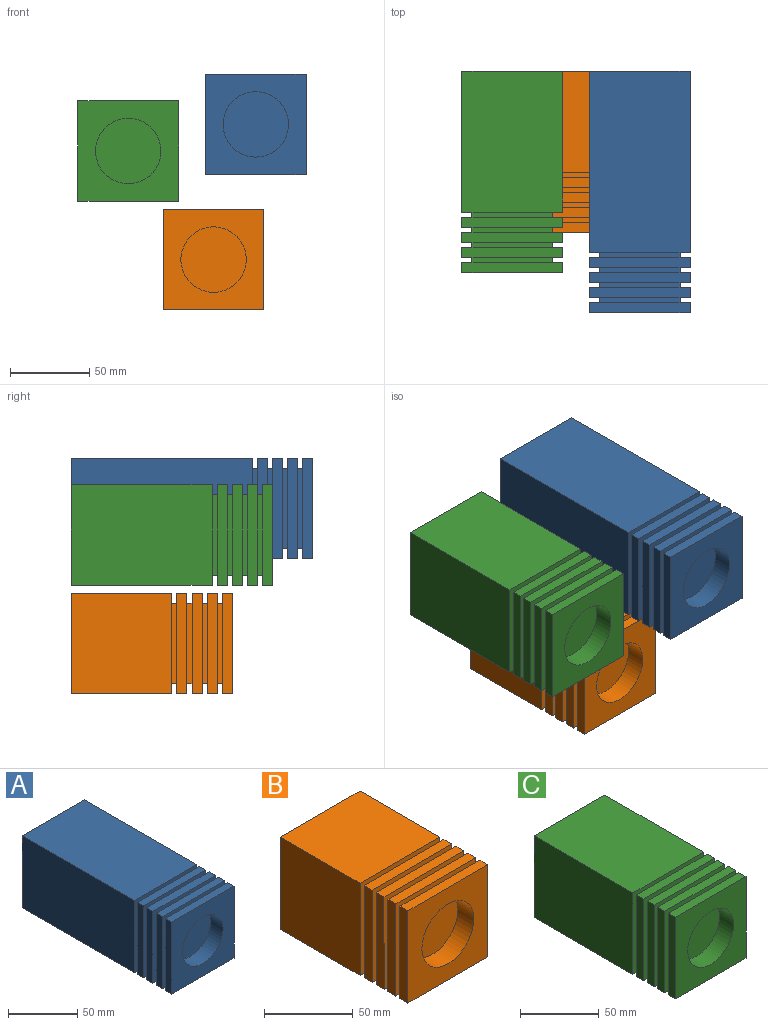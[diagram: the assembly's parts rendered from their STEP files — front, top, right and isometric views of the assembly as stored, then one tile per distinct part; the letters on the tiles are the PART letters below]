
ASSEMBLY  parts=3 mates=2
PART A: 48 faces, bbox 63.5x152.4x63.5 mm
  f0: plane 114.3x63.5mm, normal (1,0,0), area 7258.1mm2, adj f1,f2,f8,f41
  f1: plane 114.3x63.5mm, normal (0,0,-1), area 7258.1mm2, adj f0,f3,f8,f41
  f2: plane 114.3x63.5mm, normal (0,0,1), area 7258.1mm2, adj f0,f3,f8,f41
  f3: plane 114.3x63.5mm, normal (-1,0,0), area 7258.1mm2, adj f1,f2,f8,f41
  f4: plane 50.8x3.18mm, normal (0,0,1), area 161.3mm2, adj f5,f6,f7,f8
  f5: plane 50.8x3.18mm, normal (-1,0,0), area 161.3mm2, adj f4,f7,f8,f9
  f6: plane 50.8x3.18mm, normal (1,0,0), area 161.3mm2, adj f4,f7,f8,f9
  f7: plane 63.5x63.5mm, normal (0,1,0), area 1451.6mm2, adj f4,f5,f6,f9,f10,f11,f12,f13
  f8: plane 63.5x63.5mm, normal (0,-1,0), area 1451.6mm2, adj f0,f1,f2,f3,f4,f5,f6,f9
  f9: plane 50.8x3.18mm, normal (0,0,-1), area 161.3mm2, adj f5,f6,f7,f8
  f10: plane 63.5x6.35mm, normal (1,0,0), area 403.2mm2, adj f7,f11,f12,f18
  f11: plane 63.5x6.35mm, normal (0,0,-1), area 403.2mm2, adj f7,f10,f13,f18
  f12: plane 63.5x6.35mm, normal (0,0,1), area 403.2mm2, adj f7,f10,f13,f18
  f13: plane 63.5x6.35mm, normal (-1,0,0), area 403.2mm2, adj f7,f11,f12,f18
  f14: plane 50.8x3.18mm, normal (0,0,1), area 161.3mm2, adj f15,f16,f17,f18
  f15: plane 50.8x3.18mm, normal (-1,0,0), area 161.3mm2, adj f14,f17,f18,f19
  f16: plane 50.8x3.18mm, normal (1,0,0), area 161.3mm2, adj f14,f17,f18,f19
  f17: plane 63.5x63.5mm, normal (0,1,0), area 1451.6mm2, adj f14,f15,f16,f19,f20,f21,f22,f23
  f18: plane 63.5x63.5mm, normal (0,-1,0), area 1451.6mm2, adj f10,f11,f12,f13,f14,f15,f16,f19
  f19: plane 50.8x3.18mm, normal (0,0,-1), area 161.3mm2, adj f15,f16,f17,f18
  f20: plane 63.5x6.35mm, normal (1,0,0), area 403.2mm2, adj f17,f21,f22,f28
  f21: plane 63.5x6.35mm, normal (0,0,-1), area 403.2mm2, adj f17,f20,f23,f28
  f22: plane 63.5x6.35mm, normal (0,0,1), area 403.2mm2, adj f17,f20,f23,f28
  f23: plane 63.5x6.35mm, normal (-1,0,0), area 403.2mm2, adj f17,f21,f22,f28
  f24: plane 50.8x3.18mm, normal (0,0,1), area 161.3mm2, adj f25,f26,f27,f28
  f25: plane 50.8x3.18mm, normal (-1,0,0), area 161.3mm2, adj f24,f27,f28,f29
  f26: plane 50.8x3.18mm, normal (1,0,0), area 161.3mm2, adj f24,f27,f28,f29
  f27: plane 63.5x63.5mm, normal (0,1,0), area 1451.6mm2, adj f24,f25,f26,f29,f32,f34,f35,f36
  f28: plane 63.5x63.5mm, normal (0,-1,0), area 1451.6mm2, adj f20,f21,f22,f23,f24,f25,f26,f29
  f29: plane 50.8x3.18mm, normal (0,0,-1), area 161.3mm2, adj f25,f26,f27,f28
  f30: plane 63.5x6.35mm, normal (0,0,1), area 403.2mm2, adj f37,f39,f40,f44
  f31: plane 50.8x3.18mm, normal (-1,0,0), area 161.3mm2, adj f33,f44,f45,f47
  f32: plane 63.5x6.35mm, normal (-1,0,0), area 403.2mm2, adj f27,f34,f36,f45
  f33: plane 50.8x3.18mm, normal (0,0,-1), area 161.3mm2, adj f31,f44,f45,f46
  f34: plane 63.5x6.35mm, normal (0,0,1), area 403.2mm2, adj f27,f32,f35,f45
  f35: plane 63.5x6.35mm, normal (1,0,0), area 403.2mm2, adj f27,f34,f36,f45
  f36: plane 63.5x6.35mm, normal (0,0,-1), area 403.2mm2, adj f27,f32,f35,f45
  f37: plane 63.5x6.35mm, normal (-1,0,0), area 403.2mm2, adj f30,f38,f40,f44
  f38: plane 63.5x6.35mm, normal (0,0,-1), area 403.2mm2, adj f37,f39,f40,f44
  f39: plane 63.5x6.35mm, normal (1,0,0), area 403.2mm2, adj f30,f38,f40,f44
  f40: plane 63.5x63.5mm, normal (0,-1,0), area 2694.2mm2, adj f30,f37,f38,f39,f42
  f41: plane 63.5x63.5mm, normal (0,1,0), area 4032.3mm2, adj f0,f1,f2,f3
  f42: cylinder r=20.64mm len=41.28mm, axis (0,-1,0), area 1646.8mm2, adj f40,f43
  f43: plane 41.28x41.28mm, normal (0,-1,0), area 1338mm2, adj f42
  f44: plane 63.5x63.5mm, normal (0,1,0), area 1451.6mm2, adj f30,f31,f33,f37,f38,f39,f46,f47
  f45: plane 63.5x63.5mm, normal (0,-1,0), area 1451.6mm2, adj f31,f32,f33,f34,f35,f36,f46,f47
  f46: plane 50.8x3.18mm, normal (1,0,0), area 161.3mm2, adj f33,f44,f45,f47
  f47: plane 50.8x3.18mm, normal (0,0,1), area 161.3mm2, adj f31,f44,f45,f46
PART B: 48 faces, bbox 63.5x101.6x63.5 mm
  f0: plane 63.5x63.5mm, normal (1,0,0), area 4032.3mm2, adj f1,f2,f8,f41
  f1: plane 63.5x63.5mm, normal (0,0,-1), area 4032.3mm2, adj f0,f3,f8,f41
  f2: plane 63.5x63.5mm, normal (0,0,1), area 4032.3mm2, adj f0,f3,f8,f41
  f3: plane 63.5x63.5mm, normal (-1,0,0), area 4032.3mm2, adj f1,f2,f8,f41
  f4: plane 50.8x3.18mm, normal (0,0,1), area 161.3mm2, adj f5,f6,f7,f8
  f5: plane 50.8x3.18mm, normal (-1,0,0), area 161.3mm2, adj f4,f7,f8,f9
  f6: plane 50.8x3.18mm, normal (1,0,0), area 161.3mm2, adj f4,f7,f8,f9
  f7: plane 63.5x63.5mm, normal (0,1,0), area 1451.6mm2, adj f4,f5,f6,f9,f10,f11,f12,f13
  f8: plane 63.5x63.5mm, normal (0,-1,0), area 1451.6mm2, adj f0,f1,f2,f3,f4,f5,f6,f9
  f9: plane 50.8x3.18mm, normal (0,0,-1), area 161.3mm2, adj f5,f6,f7,f8
  f10: plane 63.5x6.35mm, normal (1,0,0), area 403.2mm2, adj f7,f11,f12,f18
  f11: plane 63.5x6.35mm, normal (0,0,-1), area 403.2mm2, adj f7,f10,f13,f18
  f12: plane 63.5x6.35mm, normal (0,0,1), area 403.2mm2, adj f7,f10,f13,f18
  f13: plane 63.5x6.35mm, normal (-1,0,0), area 403.2mm2, adj f7,f11,f12,f18
  f14: plane 50.8x3.18mm, normal (0,0,1), area 161.3mm2, adj f15,f16,f17,f18
  f15: plane 50.8x3.18mm, normal (-1,0,0), area 161.3mm2, adj f14,f17,f18,f19
  f16: plane 50.8x3.18mm, normal (1,0,0), area 161.3mm2, adj f14,f17,f18,f19
  f17: plane 63.5x63.5mm, normal (0,1,0), area 1451.6mm2, adj f14,f15,f16,f19,f20,f21,f22,f23
  f18: plane 63.5x63.5mm, normal (0,-1,0), area 1451.6mm2, adj f10,f11,f12,f13,f14,f15,f16,f19
  f19: plane 50.8x3.18mm, normal (0,0,-1), area 161.3mm2, adj f15,f16,f17,f18
  f20: plane 63.5x6.35mm, normal (1,0,0), area 403.2mm2, adj f17,f21,f22,f28
  f21: plane 63.5x6.35mm, normal (0,0,-1), area 403.2mm2, adj f17,f20,f23,f28
  f22: plane 63.5x6.35mm, normal (0,0,1), area 403.2mm2, adj f17,f20,f23,f28
  f23: plane 63.5x6.35mm, normal (-1,0,0), area 403.2mm2, adj f17,f21,f22,f28
  f24: plane 50.8x3.18mm, normal (0,0,1), area 161.3mm2, adj f25,f26,f27,f28
  f25: plane 50.8x3.18mm, normal (-1,0,0), area 161.3mm2, adj f24,f27,f28,f29
  f26: plane 50.8x3.18mm, normal (1,0,0), area 161.3mm2, adj f24,f27,f28,f29
  f27: plane 63.5x63.5mm, normal (0,1,0), area 1451.6mm2, adj f24,f25,f26,f29,f32,f34,f35,f36
  f28: plane 63.5x63.5mm, normal (0,-1,0), area 1451.6mm2, adj f20,f21,f22,f23,f24,f25,f26,f29
  f29: plane 50.8x3.18mm, normal (0,0,-1), area 161.3mm2, adj f25,f26,f27,f28
  f30: plane 63.5x6.35mm, normal (0,0,1), area 403.2mm2, adj f37,f39,f40,f44
  f31: plane 50.8x3.18mm, normal (-1,0,0), area 161.3mm2, adj f33,f44,f45,f47
  f32: plane 63.5x6.35mm, normal (-1,0,0), area 403.2mm2, adj f27,f34,f36,f45
  f33: plane 50.8x3.18mm, normal (0,0,-1), area 161.3mm2, adj f31,f44,f45,f46
  f34: plane 63.5x6.35mm, normal (0,0,1), area 403.2mm2, adj f27,f32,f35,f45
  f35: plane 63.5x6.35mm, normal (1,0,0), area 403.2mm2, adj f27,f34,f36,f45
  f36: plane 63.5x6.35mm, normal (0,0,-1), area 403.2mm2, adj f27,f32,f35,f45
  f37: plane 63.5x6.35mm, normal (-1,0,0), area 403.2mm2, adj f30,f38,f40,f44
  f38: plane 63.5x6.35mm, normal (0,0,-1), area 403.2mm2, adj f37,f39,f40,f44
  f39: plane 63.5x6.35mm, normal (1,0,0), area 403.2mm2, adj f30,f38,f40,f44
  f40: plane 63.5x63.5mm, normal (0,-1,0), area 2694.2mm2, adj f30,f37,f38,f39,f42
  f41: plane 63.5x63.5mm, normal (0,1,0), area 4032.3mm2, adj f0,f1,f2,f3
  f42: cylinder r=20.64mm len=41.28mm, axis (0,-1,0), area 1646.8mm2, adj f40,f43
  f43: plane 41.28x41.28mm, normal (0,-1,0), area 1338mm2, adj f42
  f44: plane 63.5x63.5mm, normal (0,1,0), area 1451.6mm2, adj f30,f31,f33,f37,f38,f39,f46,f47
  f45: plane 63.5x63.5mm, normal (0,-1,0), area 1451.6mm2, adj f31,f32,f33,f34,f35,f36,f46,f47
  f46: plane 50.8x3.18mm, normal (1,0,0), area 161.3mm2, adj f33,f44,f45,f47
  f47: plane 50.8x3.18mm, normal (0,0,1), area 161.3mm2, adj f31,f44,f45,f46
PART C: 48 faces, bbox 63.5x127x63.5 mm
  f0: plane 88.9x63.5mm, normal (1,0,0), area 5645.2mm2, adj f1,f2,f8,f41
  f1: plane 88.9x63.5mm, normal (0,0,-1), area 5645.2mm2, adj f0,f3,f8,f41
  f2: plane 88.9x63.5mm, normal (0,0,1), area 5645.2mm2, adj f0,f3,f8,f41
  f3: plane 88.9x63.5mm, normal (-1,0,0), area 5645.2mm2, adj f1,f2,f8,f41
  f4: plane 50.8x3.18mm, normal (0,0,1), area 161.3mm2, adj f5,f6,f7,f8
  f5: plane 50.8x3.18mm, normal (-1,0,0), area 161.3mm2, adj f4,f7,f8,f9
  f6: plane 50.8x3.18mm, normal (1,0,0), area 161.3mm2, adj f4,f7,f8,f9
  f7: plane 63.5x63.5mm, normal (0,1,0), area 1451.6mm2, adj f4,f5,f6,f9,f10,f11,f12,f13
  f8: plane 63.5x63.5mm, normal (0,-1,0), area 1451.6mm2, adj f0,f1,f2,f3,f4,f5,f6,f9
  f9: plane 50.8x3.18mm, normal (0,0,-1), area 161.3mm2, adj f5,f6,f7,f8
  f10: plane 63.5x6.35mm, normal (1,0,0), area 403.2mm2, adj f7,f11,f12,f18
  f11: plane 63.5x6.35mm, normal (0,0,-1), area 403.2mm2, adj f7,f10,f13,f18
  f12: plane 63.5x6.35mm, normal (0,0,1), area 403.2mm2, adj f7,f10,f13,f18
  f13: plane 63.5x6.35mm, normal (-1,0,0), area 403.2mm2, adj f7,f11,f12,f18
  f14: plane 50.8x3.18mm, normal (0,0,1), area 161.3mm2, adj f15,f16,f17,f18
  f15: plane 50.8x3.18mm, normal (-1,0,0), area 161.3mm2, adj f14,f17,f18,f19
  f16: plane 50.8x3.18mm, normal (1,0,0), area 161.3mm2, adj f14,f17,f18,f19
  f17: plane 63.5x63.5mm, normal (0,1,0), area 1451.6mm2, adj f14,f15,f16,f19,f20,f21,f22,f23
  f18: plane 63.5x63.5mm, normal (0,-1,0), area 1451.6mm2, adj f10,f11,f12,f13,f14,f15,f16,f19
  f19: plane 50.8x3.18mm, normal (0,0,-1), area 161.3mm2, adj f15,f16,f17,f18
  f20: plane 63.5x6.35mm, normal (1,0,0), area 403.2mm2, adj f17,f21,f22,f28
  f21: plane 63.5x6.35mm, normal (0,0,-1), area 403.2mm2, adj f17,f20,f23,f28
  f22: plane 63.5x6.35mm, normal (0,0,1), area 403.2mm2, adj f17,f20,f23,f28
  f23: plane 63.5x6.35mm, normal (-1,0,0), area 403.2mm2, adj f17,f21,f22,f28
  f24: plane 50.8x3.18mm, normal (0,0,1), area 161.3mm2, adj f25,f26,f27,f28
  f25: plane 50.8x3.18mm, normal (-1,0,0), area 161.3mm2, adj f24,f27,f28,f29
  f26: plane 50.8x3.18mm, normal (1,0,0), area 161.3mm2, adj f24,f27,f28,f29
  f27: plane 63.5x63.5mm, normal (0,1,0), area 1451.6mm2, adj f24,f25,f26,f29,f32,f34,f35,f36
  f28: plane 63.5x63.5mm, normal (0,-1,0), area 1451.6mm2, adj f20,f21,f22,f23,f24,f25,f26,f29
  f29: plane 50.8x3.18mm, normal (0,0,-1), area 161.3mm2, adj f25,f26,f27,f28
  f30: plane 63.5x6.35mm, normal (0,0,1), area 403.2mm2, adj f37,f39,f40,f44
  f31: plane 50.8x3.18mm, normal (-1,0,0), area 161.3mm2, adj f33,f44,f45,f47
  f32: plane 63.5x6.35mm, normal (-1,0,0), area 403.2mm2, adj f27,f34,f36,f45
  f33: plane 50.8x3.18mm, normal (0,0,-1), area 161.3mm2, adj f31,f44,f45,f46
  f34: plane 63.5x6.35mm, normal (0,0,1), area 403.2mm2, adj f27,f32,f35,f45
  f35: plane 63.5x6.35mm, normal (1,0,0), area 403.2mm2, adj f27,f34,f36,f45
  f36: plane 63.5x6.35mm, normal (0,0,-1), area 403.2mm2, adj f27,f32,f35,f45
  f37: plane 63.5x6.35mm, normal (-1,0,0), area 403.2mm2, adj f30,f38,f40,f44
  f38: plane 63.5x6.35mm, normal (0,0,-1), area 403.2mm2, adj f37,f39,f40,f44
  f39: plane 63.5x6.35mm, normal (1,0,0), area 403.2mm2, adj f30,f38,f40,f44
  f40: plane 63.5x63.5mm, normal (0,-1,0), area 2694.2mm2, adj f30,f37,f38,f39,f42
  f41: plane 63.5x63.5mm, normal (0,1,0), area 4032.3mm2, adj f0,f1,f2,f3
  f42: cylinder r=20.64mm len=41.28mm, axis (0,-1,0), area 1646.8mm2, adj f40,f43
  f43: plane 41.28x41.28mm, normal (0,-1,0), area 1338mm2, adj f42
  f44: plane 63.5x63.5mm, normal (0,1,0), area 1451.6mm2, adj f30,f31,f33,f37,f38,f39,f46,f47
  f45: plane 63.5x63.5mm, normal (0,-1,0), area 1451.6mm2, adj f31,f32,f33,f34,f35,f36,f46,f47
  f46: plane 50.8x3.18mm, normal (1,0,0), area 161.3mm2, adj f33,f44,f45,f47
  f47: plane 50.8x3.18mm, normal (0,0,1), area 161.3mm2, adj f31,f44,f45,f46
PLACE A t=(-0.27,83.04,50.45)mm
PLACE B t=(-26.91,83.04,-34.91)mm
PLACE C t=(-80.79,83.04,33.63)mm
MATE planar A.f42 <-> B.f42  axis (0,1,0) through (31.48,83.04,82.2)mm
MATE planar A.f42 <-> C.f42  axis (0,1,0) through (31.48,83.04,82.2)mm
